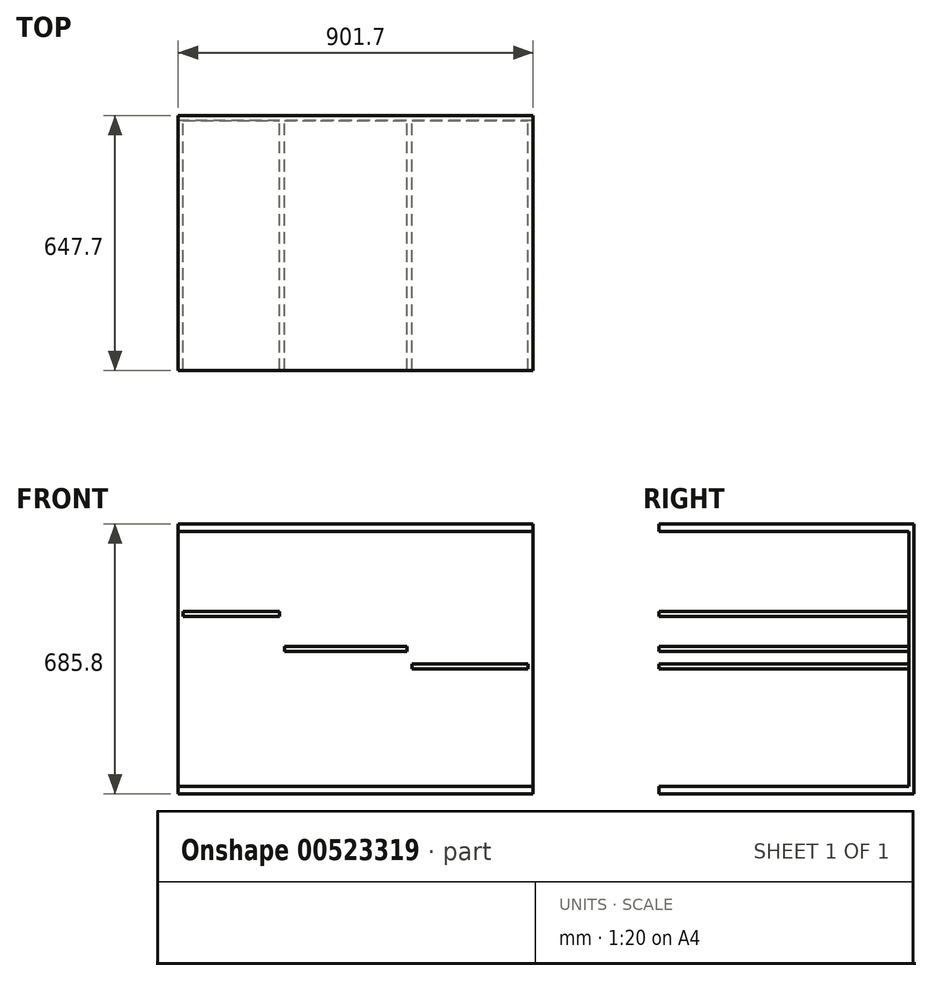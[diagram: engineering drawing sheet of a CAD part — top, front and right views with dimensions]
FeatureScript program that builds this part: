
annotation { "Feature Type Name" : "Feature", "Feature Type Description" : "" }
export const myFeature = defineFeature(function(context is Context, id is Id, definition is map)
    precondition{}
    {
        {
            var Q0;
            Q0=qCreatedBy(makeId("Front.planeOp"),FACE);
            var sketch = newSketch(context, id + "F0", { "sketchPlane" : qUnion([Q0])});
            skLineSegment(sketch, "E0.bottom", {"start": v(450.85, 9.53) * mm, "end": v(-450.85, 9.53) * mm});
            skLineSegment(sketch, "E0.top", {"start": v(450.85, -9.53) * mm, "end": v(-450.85, -9.53) * mm});
            skLineSegment(sketch, "E0.left", {"start": v(450.85, 9.53) * mm, "end": v(450.85, -9.53) * mm});
            skLineSegment(sketch, "E0.right", {"start": v(-450.85, 9.52) * mm, "end": v(-450.85, -9.53) * mm});
            skPoint(sketch, "E0.middle", {"position": v(0, 0) * mm});
            skLineSegment(sketch, "E1.bottom", {"start": v(-450.85, 9.52) * mm, "end": v(-438.15, 9.52) * mm});
            skLineSegment(sketch, "E1.top", {"start": v(-450.85, 657.23) * mm, "end": v(-438.15, 657.23) * mm});
            skLineSegment(sketch, "E1.left", {"start": v(-450.85, 9.52) * mm, "end": v(-450.85, 657.23) * mm});
            skLineSegment(sketch, "E1.right", {"start": v(-438.15, 9.52) * mm, "end": v(-438.15, 657.23) * mm});
            skLineSegment(sketch, "E2.bottom", {"start": v(-450.85, 657.23) * mm, "end": v(450.85, 657.23) * mm});
            skLineSegment(sketch, "E2.top", {"start": v(-450.85, 676.28) * mm, "end": v(450.85, 676.28) * mm});
            skLineSegment(sketch, "E2.left", {"start": v(-450.85, 657.23) * mm, "end": v(-450.85, 676.28) * mm});
            skLineSegment(sketch, "E2.right", {"start": v(450.85, 657.23) * mm, "end": v(450.85, 676.28) * mm});
            skLineSegment(sketch, "E3.bottom", {"start": v(450.85, 657.23) * mm, "end": v(438.15, 657.23) * mm});
            skLineSegment(sketch, "E3.top", {"start": v(450.85, 9.53) * mm, "end": v(438.15, 9.53) * mm});
            skLineSegment(sketch, "E3.left", {"start": v(450.85, 657.23) * mm, "end": v(450.85, 9.53) * mm});
            skLineSegment(sketch, "E3.right", {"start": v(438.15, 657.23) * mm, "end": v(438.15, 9.53) * mm});
            skLineSegment(sketch, "E4.bottom", {"start": v(-193.67, 9.53) * mm, "end": v(-180.97, 9.53) * mm});
            skLineSegment(sketch, "E4.top", {"start": v(-193.68, 657.23) * mm, "end": v(-180.98, 657.23) * mm});
            skLineSegment(sketch, "E4.left", {"start": v(-193.67, 9.53) * mm, "end": v(-193.68, 657.23) * mm});
            skLineSegment(sketch, "E4.right", {"start": v(-180.97, 9.53) * mm, "end": v(-180.98, 657.23) * mm});
            skLineSegment(sketch, "E5.bottom", {"start": v(130.17, 657.23) * mm, "end": v(142.87, 657.23) * mm});
            skLineSegment(sketch, "E5.top", {"start": v(130.17, 9.53) * mm, "end": v(142.87, 9.53) * mm});
            skLineSegment(sketch, "E5.left", {"start": v(130.17, 657.23) * mm, "end": v(130.17, 9.53) * mm});
            skLineSegment(sketch, "E5.right", {"start": v(142.87, 657.23) * mm, "end": v(142.87, 9.53) * mm});
            skLineSegment(sketch, "E6.bottom", {"start": v(-438.15, 441.33) * mm, "end": v(-193.68, 441.33) * mm});
            skLineSegment(sketch, "E6.top", {"start": v(-438.15, 454.03) * mm, "end": v(-193.68, 454.03) * mm});
            skLineSegment(sketch, "E6.left", {"start": v(-438.15, 441.33) * mm, "end": v(-438.15, 454.03) * mm});
            skLineSegment(sketch, "E6.right", {"start": v(-193.68, 441.33) * mm, "end": v(-193.68, 454.03) * mm});
            skLineSegment(sketch, "E7.bottom", {"start": v(-180.98, 352.43) * mm, "end": v(130.17, 352.43) * mm});
            skLineSegment(sketch, "E7.top", {"start": v(-180.98, 365.13) * mm, "end": v(130.17, 365.13) * mm});
            skLineSegment(sketch, "E7.left", {"start": v(-180.98, 352.43) * mm, "end": v(-180.98, 365.13) * mm});
            skLineSegment(sketch, "E7.right", {"start": v(130.17, 352.43) * mm, "end": v(130.17, 365.13) * mm});
            skLineSegment(sketch, "E8.bottom", {"start": v(142.87, 320.68) * mm, "end": v(438.15, 320.68) * mm});
            skLineSegment(sketch, "E8.top", {"start": v(142.87, 307.98) * mm, "end": v(438.15, 307.98) * mm});
            skLineSegment(sketch, "E8.left", {"start": v(142.87, 320.68) * mm, "end": v(142.87, 307.98) * mm});
            skLineSegment(sketch, "E8.right", {"start": v(438.15, 320.68) * mm, "end": v(438.15, 307.98) * mm});
            skSolve(sketch);
        }
        {
            var Q0;
            {var subQ4=sQuery(id+"F0.wireOp",EDGE,"E1.bottom");Q0=makeQuery(id+"F0.imprint","IMPRINT",FACE,{"disambiguationData":[TD([[makeQuery(id+"F0.imprint","IMPRINT",EDGE,{"derivedFrom":subQ4}),1.0]])]});}
            var Q1;
            Q1=makeQuery(id+"F0.imprint","IMPRINT",FACE,{"disambiguationData":[TD([[makeQuery(id+"F0.imprint","IMPRINT",EDGE,{"derivedFrom":sQuery(id+"F0.wireOp",EDGE,"E2.top")}),-1.0]])]});
            var Q2;
            {var subQ4=sQuery(id+"F0.wireOp",EDGE,"E4.bottom");Q2=makeQuery(id+"F0.imprint","IMPRINT",FACE,{"disambiguationData":[TD([[makeQuery(id+"F0.imprint","IMPRINT",EDGE,{"derivedFrom":subQ4}),1.0]])]});}
            var Q3;
            Q3=makeQuery(id+"F0.imprint","IMPRINT",FACE,{"disambiguationData":[TD([[makeQuery(id+"F0.imprint","IMPRINT",EDGE,{"derivedFrom":sQuery(id+"F0.wireOp",EDGE,"E6.bottom")}),1.0]])]});
            var Q4;
            Q4=makeQuery(id+"F0.imprint","IMPRINT",FACE,{"disambiguationData":[TD([[makeQuery(id+"F0.imprint","IMPRINT",EDGE,{"derivedFrom":sQuery(id+"F0.wireOp",EDGE,"E7.bottom")}),1.0]])]});
            var Q5;
            {var subQ4=sQuery(id+"F0.wireOp",EDGE,"E5.bottom");Q5=makeQuery(id+"F0.imprint","IMPRINT",FACE,{"disambiguationData":[TD([[makeQuery(id+"F0.imprint","IMPRINT",EDGE,{"derivedFrom":subQ4}),-1.0]])]});}
            var Q6;
            Q6=makeQuery(id+"F0.imprint","IMPRINT",FACE,{"disambiguationData":[TD([[makeQuery(id+"F0.imprint","IMPRINT",EDGE,{"derivedFrom":sQuery(id+"F0.wireOp",EDGE,"E8.bottom")}),-1.0]])]});
            var Q7;
            {var subQ1=sQuery(id+"F0.wireOp",EDGE,"E3.bottom");Q7=makeQuery(id+"F0.imprint","IMPRINT",FACE,{"disambiguationData":[TD([[makeQuery(id+"F0.imprint","IMPRINT",EDGE,{"derivedFrom":subQ1}),1.0]])]});}
            var Q8;
            Q8=makeQuery(id+"F0.imprint","IMPRINT",FACE,{"disambiguationData":[TD([[makeQuery(id+"F0.imprint","IMPRINT",EDGE,{"derivedFrom":sQuery(id+"F0.wireOp",EDGE,"E0.top")}),-1.0]])]});
            extrude(context, id + "F1", {"entities" : qUnion([Q0, Q1, Q2, Q3, Q4, Q5, Q6, Q7, Q8]), "depth" : 635 * mm, "offsetDistance" : 25.4 * mm});
        }
        {
            var Q0;
            Q0=makeQuery(id+"F1.opExtrude","CAP_FACE",FACE,{"disambiguationData":[OSD([sQuery(id+"F0.wireOp",EDGE,"E0.bottom"),sQuery(id+"F0.wireOp",EDGE,"E0.top"),sQuery(id+"F0.wireOp",EDGE,"E0.left"),sQuery(id+"F0.wireOp",EDGE,"E0.right"),sQuery(id+"F0.wireOp",EDGE,"E1.left"),sQuery(id+"F0.wireOp",EDGE,"E1.right"),sQuery(id+"F0.wireOp",EDGE,"E2.bottom"),sQuery(id+"F0.wireOp",EDGE,"E2.top"),sQuery(id+"F0.wireOp",EDGE,"E2.left"),sQuery(id+"F0.wireOp",EDGE,"E2.right"),sQuery(id+"F0.wireOp",EDGE,"E3.left"),sQuery(id+"F0.wireOp",EDGE,"E3.right"),sQuery(id+"F0.wireOp",EDGE,"E4.left"),sQuery(id+"F0.wireOp",EDGE,"E4.right"),sQuery(id+"F0.wireOp",EDGE,"E5.left"),sQuery(id+"F0.wireOp",EDGE,"E5.right"),sQuery(id+"F0.wireOp",EDGE,"E6.bottom"),sQuery(id+"F0.wireOp",EDGE,"E6.top"),sQuery(id+"F0.wireOp",EDGE,"E7.bottom"),sQuery(id+"F0.wireOp",EDGE,"E7.top"),sQuery(id+"F0.wireOp",EDGE,"E8.bottom"),sQuery(id+"F0.wireOp",EDGE,"E8.top")])],"isStart":true});
            var sketch = newSketch(context, id + "F2", { "sketchPlane" : qUnion([Q0])});
            skLineSegment(sketch, "E9.bottom", {"start": v(-450.85, -9.53) * mm, "end": v(450.85, -9.53) * mm});
            skLineSegment(sketch, "E9.top", {"start": v(-450.85, 676.28) * mm, "end": v(450.85, 676.28) * mm});
            skLineSegment(sketch, "E9.left", {"start": v(-450.85, -9.53) * mm, "end": v(-450.85, 676.28) * mm});
            skLineSegment(sketch, "E9.right", {"start": v(450.85, -9.53) * mm, "end": v(450.85, 676.28) * mm});
            skSolve(sketch);
        }
        {
            var Q0;
            Q0 = qSketchRegion(id + "F2", true);
            extrude(context, id + "F3", {"entities" : qUnion([Q0]), "operationType" : NewBodyOperationType.ADD, "depth" : 12.7 * mm, "offsetDistance" : 25.4 * mm});
        }
    });
